# Revit family: Hager-Orion_Inox-IP66-D150-Cl.I-Inox_encl-630A-300mm-NoHosted-PL-pl
name_source: partatom
category: Equipement électrique
units: mm (PartAtom-declared; Revit-internal decimal feet)

## family parameters
Basée sur le plan de construction = Oui
Configuration du panneau = Deux colonnes, circuits au sein
Cote de connecteur circulaire = Utiliser le diamètre
Couper avec des vides une fois chargée = Non
Partagée = Non
Point de calcul de pièce = Non
Toujours verticalement = Oui
Type d'élément = Tableau de raccordement

## types (4) — shared parameters
Commentaires du type = Orion Inox
EF000003 - Sposób montażu = EV000384 - Montaż natynkowy
EF000007 - Kolor = EV000154 - Inne
EF000040 - Wysokość = 300 mm
EF000049 - Głębokość = 150 mm  [stored 0.492126 ft]
EF000118 - Z płytą montażową = Non
EF000339 - Rodzaj pokrywy = EV004216 - Drzwi
EF001088 - Możliwość rozbudowy = Oui
EF001131 - Głębokość wewnętrzna = 116 mm  [stored 0.380577 ft]
EF001596 - Materiał obudowy = EV000166 - Stal nierdzewna
EF003532 - Do zastosowań zewnętrznych = Oui
EF004293 - Odporność udarowa = EV008784 - IK10
EF004464 - Rodzaj drzwi = EV002646 - Pojedynczy
EF005474 - Stopień ochrony (IP) = EV006422 - IP66
EF006244 - Transparentna pokrywa/drzwi = Non
EF007800 - Do ochrony odgromowej = Non
EF008873 - Prąd znamionowy (In) = 630 A
EF009170 - Obudowa z materiału o wysokiej wytrzymałości mechanicznej = 2 mm  [stored 0.00656168 ft]
EF009171 - Drzwi/pokrywa z materiału o wysokiej wytrzymałości mechanicznej = 2 mm  [stored 0.00656168 ft]
EF015940 - Pokrywa z wyzwalaczem nadciśnieniowym = Non
Elévation par défaut = 1219 mm
Fabricant = Hager
HG000002 - Z drzwiami lub pokrywą = Oui
HG000003 - Zakres = Orion Inox
HG000006 - Montaż podtynkowy = Non
HG000009 - Drzwi dwuskrzydłowe = Non
HG000010 - Drzwi asymetryczne = Non
HG000023 - Obudowa dwusekcyjna = Non
HG000024 - Wysokość części dolnej = 600 mm
HG000026 - Stojąca = Non
zero-valued in all types: EF000218 - Głębokość wbudowania, EF000266 - Liczba rzędów, EF000437 - Liczba wejść kablowych, EF002950 - Szerokość wyrażona liczbą modułów, EF004427 - Liczba modułów, EF009554 - Liczba otworów pod flansze, HG000027 - Wysokość cokołu

## per-type parameters (varying)
| type | EF000008 - Szerokość | EF001613 - Podtrzymanie funkcji | EF006306 - Z zamkiem | EF009212 - Wykonanie pokrywy | HG000004 - Referencja producenta |
| Montaż natynkowy IP66 S200 W300 G150  - FL010BW | 200 mm  [stored 0.656168 ft] |  | Non | EV009916 - Z otworem | FL010BW |
| Montaż natynkowy IP66 S200 W300 G150  - FL010BWL | 200 mm  [stored 0.656168 ft] |  | Non | EV009916 - Z otworem | FL010BWL |
| Montaż natynkowy IP66 S400 W300 G150  - FL013BW | 400 mm  [stored 1.31234 ft] | EV000494 - Brak | Oui | EV000116 - Zamknięty | FL013BW |
| Montaż natynkowy IP66 S400 W300 G150  - FL013BWL | 400 mm  [stored 1.31234 ft] | EV000494 - Brak | Oui | EV000116 - Zamknięty | FL013BWL |

note: [stored X ft] marks values corroborated as IEEE doubles in the binary element streams (Revit-internal decimal feet)

## geometry (parser evidence)
native form markers: Blend x4, Sweep x8
no freeform markers — native parametric forms only
